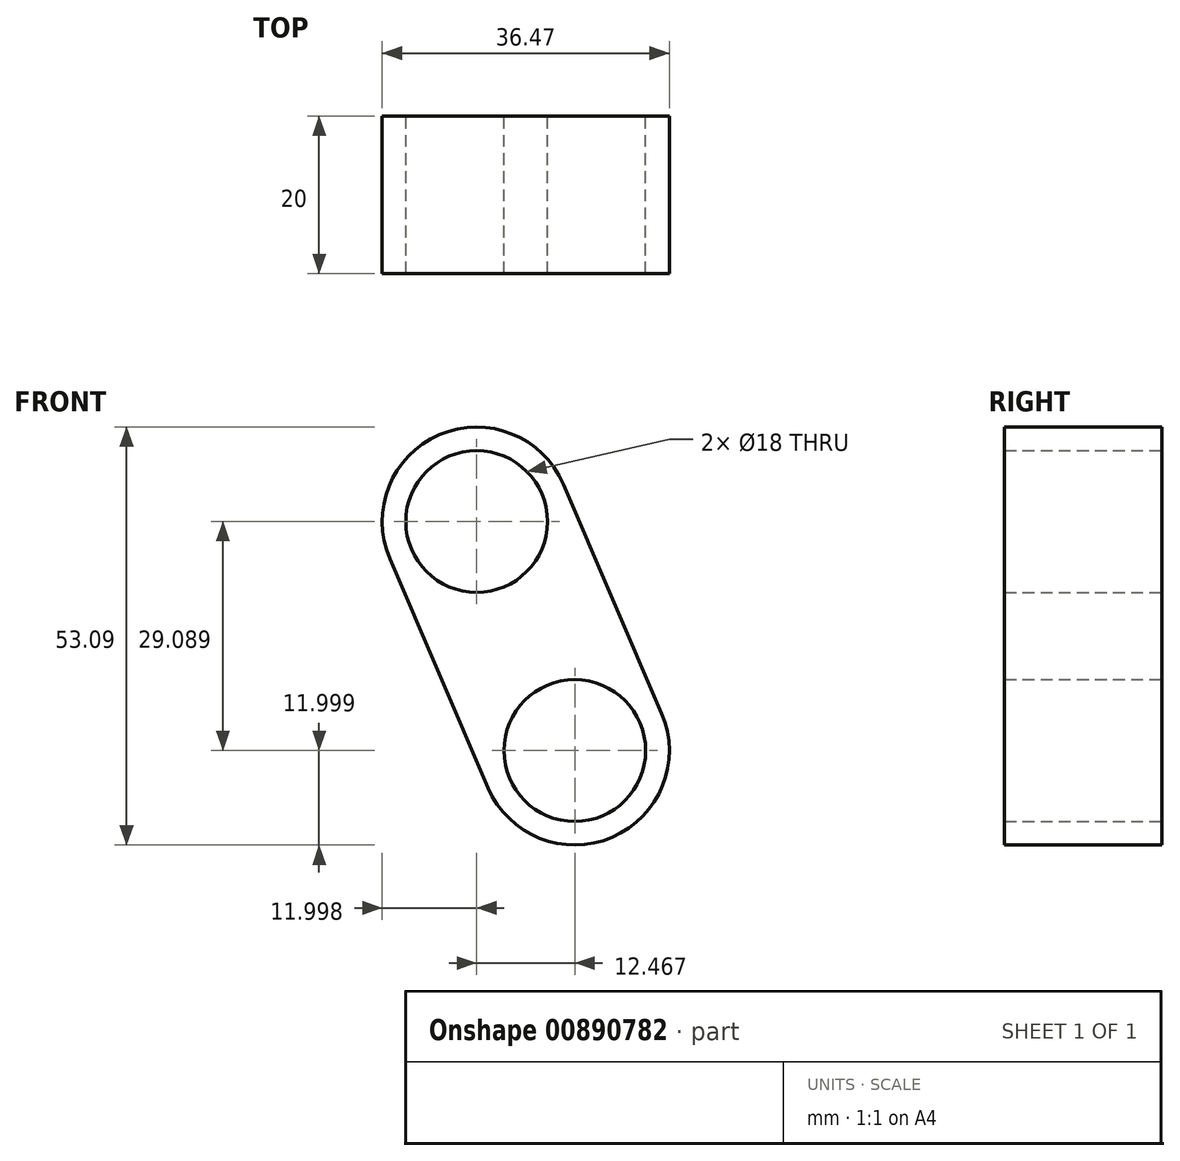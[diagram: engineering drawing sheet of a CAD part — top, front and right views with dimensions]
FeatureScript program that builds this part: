
annotation { "Feature Type Name" : "Feature", "Feature Type Description" : "" }
export const myFeature = defineFeature(function(context is Context, id is Id, definition is map)
    precondition{}
    {
        {
            var Q0;
            Q0=qCreatedBy(makeId("Front.planeOp"),FACE);
            var sketch = newSketch(context, id + "F0", { "sketchPlane" : qUnion([Q0])});
            skLineSegment(sketch, "E0", {"start": v(0, 0) * mm, "end": v(395.95, 0) * mm});
            skLineSegment(sketch, "E1", {"start": v(388.52, 1.06) * mm, "end": v(20.19, 53.9) * mm});
            skLineSegment(sketch, "E2.MirrorCS", {"start": v(388.52, -1.06) * mm, "end": v(4.53, -56.14) * mm});
            skCircle(sketch, "E3", {"center": v(395.95, 0) * mm, "radius": 7.5 * mm});
            skLineSegment(sketch, "E4", {"start": v(0, 56.8) * mm, "end": v(0.85, 62.73) * mm});
            skLineSegment(sketch, "E5", {"start": v(0.85, 62.73) * mm, "end": v(2.93, 62.44) * mm});
            skLineSegment(sketch, "E6", {"start": v(1.3, 60.65) * mm, "end": v(0.57, 60.75) * mm});
            skLineSegment(sketch, "E7.MirrorCS", {"start": v(390.24, -4.86) * mm, "end": v(9.54, -59.47) * mm});
            skCircle(sketch, "E8", {"center": v(9.43, 42.25) * mm, "radius": 9 * mm});
            skCircle(sketch, "E9", {"center": v(-47.08, -35.04) * mm, "radius": 9 * mm});
            skCircle(sketch, "E10", {"center": v(-59.55, -5.95) * mm, "radius": 9 * mm});
            skCircle(sketch, "E11", {"center": v(12.76, 73.42) * mm, "radius": 3.72 * mm});
            skArc(sketch, "E12", {"start": v(19.8, 72.67) * mm, "mid": v(13.5, 80.46) * mm, "end": v(5.72, 74.17) * mm});
            skArc(sketch, "E13", {"start": v(15.73, 33.24) * mm, "mid": v(19.24, 37.27) * mm, "end": v(20.43, 42.48) * mm});
            skCircle(sketch, "E14", {"center": v(7.04, -66.2) * mm, "radius": 5 * mm});
            skLineSegment(sketch, "E15.trimOffspring", {"start": v(11.9, -61.15) * mm, "end": v(392.34, -6.58) * mm});
            skLineSegment(sketch, "E16", {"start": v(10.54, -60.13) * mm, "end": v(4.53, -56.14) * mm});
            skPoint(sketch, "E17.orphan", {"position": v(0, -78.43) * mm});
            skPoint(sketch, "E18.trimOffspring.end.orphan", {"position": v(-61.82, -60.65) * mm});
            skArc(sketch, "E19", {"start": v(3.94, -72.47) * mm, "mid": v(13.22, -69.5) * mm, "end": v(10.54, -60.13) * mm});
            skLineSegment(sketch, "E20", {"start": v(3.55, -72.27) * mm, "end": v(3.94, -72.47) * mm});
            skLineSegment(sketch, "E21", {"start": v(19.8, 72.67) * mm, "end": v(20.43, 42.48) * mm});
            skLineSegment(sketch, "E22", {"start": v(5.72, 74.17) * mm, "end": v(-0.8, 46.75) * mm});
            skLineSegment(sketch, "E23.trimOffspring", {"start": v(20.06, 59.98) * mm, "end": v(392.34, 6.58) * mm});
            skLineSegment(sketch, "E24.trimOffspring", {"start": v(2.46, 60.48) * mm, "end": v(0.85, 60.71) * mm});
            skLineSegment(sketch, "E25.trimOffspring", {"start": v(1.53, 56.58) * mm, "end": v(0, 56.8) * mm});
            skPoint(sketch, "E26.visualSharp", {"position": v(-1.27, 44.8) * mm});
            skArc(sketch, "E26.filletArc", {"start": v(-2.96, 43.7) * mm, "mid": v(-1.59, 45.02) * mm, "end": v(-0.8, 46.75) * mm});
            skLineSegment(sketch, "E27.trimOffspring", {"start": v(2.7, -63.7) * mm, "end": v(7.04, -66.2) * mm});
            skArc(sketch, "E28", {"start": v(-48.52, -1.23) * mm, "mid": v(-64.28, 5.08) * mm, "end": v(-70.58, -10.68) * mm});
            skArc(sketch, "E29", {"start": v(-58.11, -39.77) * mm, "mid": v(-42.36, -46.07) * mm, "end": v(-36.06, -30.31) * mm});
            skLineSegment(sketch, "E30", {"start": v(-70.58, -10.68) * mm, "end": v(-58.11, -39.77) * mm});
            skLineSegment(sketch, "E31.MirrorCS", {"start": v(-48.52, -1.23) * mm, "end": v(-36.06, -30.31) * mm});
            skSolve(sketch);
        }
        {
            var Q0;
            Q0=makeQuery(id+"F0.imprint","IMPRINT",FACE,{"disambiguationData":[TD([[makeQuery(id+"F0.imprint","IMPRINT",EDGE,{"derivedFrom":sQuery(id+"F0.wireOp",EDGE,"E9")}),-1.0]])]});
            extrude(context, id + "F1", {"entities" : qUnion([Q0]), "depth" : 20 * mm, "offsetDistance" : 25 * mm});
        }
    });
